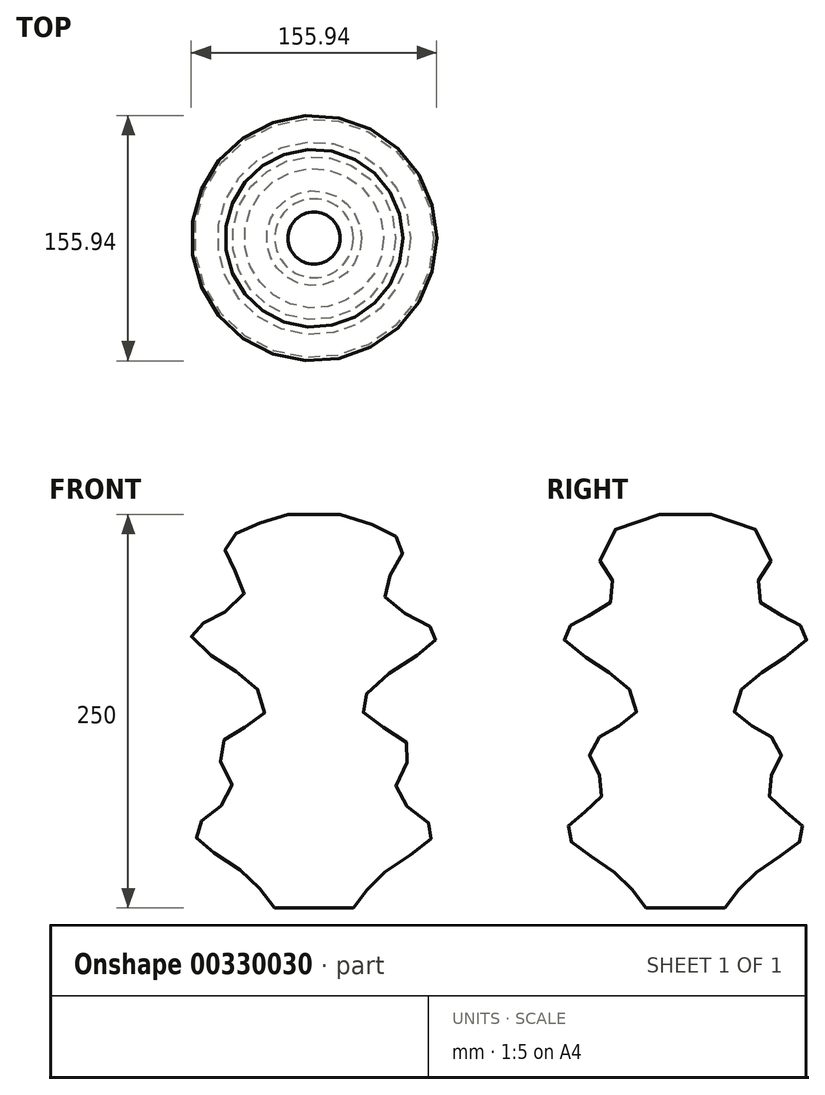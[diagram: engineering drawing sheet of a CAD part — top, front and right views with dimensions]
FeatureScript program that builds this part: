
annotation { "Feature Type Name" : "Feature", "Feature Type Description" : "" }
export const myFeature = defineFeature(function(context is Context, id is Id, definition is map)
    precondition{}
    {
        {
            var Q0;
            Q0=qCreatedBy(makeId("Top.planeOp"),FACE);
            cPlane(context, id + "F0", {"entities" : qUnion([Q0]), "cplaneType" : CPlaneType.OFFSET, "offset" : 25 * mm, "width" : 150 * mm, "height" : 150 * mm});
        }
        {
            var Q0;
            Q0=qCreatedBy(id+"F0.planeOp",FACE);
            cPlane(context, id + "F1", {"entities" : qUnion([Q0]), "cplaneType" : CPlaneType.OFFSET, "offset" : 25 * mm, "width" : 150 * mm, "height" : 150 * mm});
        }
        {
            var Q0;
            Q0=qCreatedBy(id+"F1.planeOp",FACE);
            cPlane(context, id + "F2", {"entities" : qUnion([Q0]), "cplaneType" : CPlaneType.OFFSET, "offset" : 25 * mm, "width" : 150 * mm, "height" : 150 * mm});
        }
        {
            var Q0;
            Q0=qCreatedBy(id+"F2.planeOp",FACE);
            cPlane(context, id + "F3", {"entities" : qUnion([Q0]), "cplaneType" : CPlaneType.OFFSET, "offset" : 25 * mm, "width" : 150 * mm, "height" : 150 * mm});
        }
        {
            var Q0;
            Q0=qCreatedBy(id+"F3.planeOp",FACE);
            cPlane(context, id + "F4", {"entities" : qUnion([Q0]), "cplaneType" : CPlaneType.OFFSET, "offset" : 25 * mm, "width" : 150 * mm, "height" : 150 * mm});
        }
        {
            var Q0;
            Q0=qCreatedBy(id+"F4.planeOp",FACE);
            cPlane(context, id + "F5", {"entities" : qUnion([Q0]), "cplaneType" : CPlaneType.OFFSET, "offset" : 25 * mm, "width" : 150 * mm, "height" : 150 * mm});
        }
        {
            var Q0;
            Q0=qCreatedBy(id+"F5.planeOp",FACE);
            cPlane(context, id + "F6", {"entities" : qUnion([Q0]), "cplaneType" : CPlaneType.OFFSET, "offset" : 25 * mm, "width" : 150 * mm, "height" : 150 * mm});
        }
        {
            var Q0;
            Q0=qCreatedBy(id+"F6.planeOp",FACE);
            cPlane(context, id + "F7", {"entities" : qUnion([Q0]), "cplaneType" : CPlaneType.OFFSET, "offset" : 25 * mm, "width" : 150 * mm, "height" : 150 * mm});
        }
        {
            var Q0;
            Q0=qCreatedBy(id+"F7.planeOp",FACE);
            cPlane(context, id + "F8", {"entities" : qUnion([Q0]), "cplaneType" : CPlaneType.OFFSET, "offset" : 25 * mm, "width" : 150 * mm, "height" : 150 * mm});
        }
        {
            var Q0;
            Q0=qCreatedBy(id+"F8.planeOp",FACE);
            cPlane(context, id + "F9", {"entities" : qUnion([Q0]), "cplaneType" : CPlaneType.OFFSET, "offset" : 25 * mm, "width" : 150 * mm, "height" : 150 * mm});
        }
        {
            var Q0;
            Q0=qCreatedBy(makeId("Top.planeOp"),FACE);
            var sketch = newSketch(context, id + "F10", { "sketchPlane" : qUnion([Q0])});
            skCircle(sketch, "E0", {"center": v(0, 0) * mm, "radius": 25 * mm});
            skSolve(sketch);
        }
        {
            var Q0;
            Q0=qCreatedBy(id+"F0.planeOp",FACE);
            var sketch = newSketch(context, id + "F11", { "sketchPlane" : qUnion([Q0])});
            skCircle(sketch, "E1", {"center": v(0, 0) * mm, "radius": 48 * mm});
            skSolve(sketch);
        }
        {
            var Q0;
            Q0=qCreatedBy(id+"F1.planeOp",FACE);
            var sketch = newSketch(context, id + "F12", { "sketchPlane" : qUnion([Q0])});
            skCircle(sketch, "E2", {"center": v(0, 0) * mm, "radius": 75.7 * mm});
            skSolve(sketch);
        }
        {
            var Q0;
            Q0=qCreatedBy(id+"F2.planeOp",FACE);
            var sketch = newSketch(context, id + "F13", { "sketchPlane" : qUnion([Q0])});
            skCircle(sketch, "E3", {"center": v(0, 0) * mm, "radius": 51.88 * mm});
            skSolve(sketch);
        }
        {
            var Q0;
            Q0=qCreatedBy(id+"F3.planeOp",FACE);
            var sketch = newSketch(context, id + "F14", { "sketchPlane" : qUnion([Q0])});
            skCircle(sketch, "E4", {"center": v(0, 0) * mm, "radius": 61.23 * mm});
            skSolve(sketch);
        }
        {
            var Q0;
            Q0=qCreatedBy(id+"F4.planeOp",FACE);
            var sketch = newSketch(context, id + "F15", { "sketchPlane" : qUnion([Q0])});
            skCircle(sketch, "E5", {"center": v(0, 0) * mm, "radius": 30.87 * mm});
            skSolve(sketch);
        }
        {
            var Q0;
            Q0=qCreatedBy(id+"F5.planeOp",FACE);
            var sketch = newSketch(context, id + "F16", { "sketchPlane" : qUnion([Q0])});
            skCircle(sketch, "E6", {"center": v(0, 0) * mm, "radius": 49.04 * mm});
            skSolve(sketch);
        }
        {
            var Q0;
            Q0=qCreatedBy(id+"F6.planeOp",FACE);
            var sketch = newSketch(context, id + "F17", { "sketchPlane" : qUnion([Q0])});
            skCircle(sketch, "E7", {"center": v(0, 0) * mm, "radius": 77.58 * mm});
            skSolve(sketch);
        }
        {
            var Q0;
            Q0=qCreatedBy(id+"F7.planeOp",FACE);
            var sketch = newSketch(context, id + "F18", { "sketchPlane" : qUnion([Q0])});
            skCircle(sketch, "E8", {"center": v(0, 0) * mm, "radius": 44.38 * mm});
            skSolve(sketch);
        }
        {
            var Q0;
            Q0=qCreatedBy(id+"F8.planeOp",FACE);
            var sketch = newSketch(context, id + "F19", { "sketchPlane" : qUnion([Q0])});
            skCircle(sketch, "E9", {"center": v(0, 0) * mm, "radius": 56.04 * mm});
            skSolve(sketch);
        }
        {
            var Q0;
            Q0=qCreatedBy(id+"F9.planeOp",FACE);
            var sketch = newSketch(context, id + "F20", { "sketchPlane" : qUnion([Q0])});
            skCircle(sketch, "E10", {"center": v(0, 0) * mm, "radius": 16.55 * mm});
            skSolve(sketch);
        }
        {
            var Q0;
            Q0=makeQuery(id+"F10.imprint","IMPRINT",FACE,{"disambiguationData":[TD([[makeQuery(id+"F10.imprint","IMPRINT",EDGE,{"derivedFrom":sQuery(id+"F10.wireOp",EDGE,"E0")}),1.0]])]});
            var Q1;
            Q1=makeQuery(id+"F11.imprint","IMPRINT",FACE,{"disambiguationData":[TD([[makeQuery(id+"F11.imprint","IMPRINT",EDGE,{"derivedFrom":sQuery(id+"F11.wireOp",EDGE,"E1")}),1.0]])]});
            var Q2;
            Q2=makeQuery(id+"F12.imprint","IMPRINT",FACE,{"disambiguationData":[TD([[makeQuery(id+"F12.imprint","IMPRINT",EDGE,{"derivedFrom":sQuery(id+"F12.wireOp",EDGE,"E2")}),1.0]])]});
            var Q3;
            Q3=makeQuery(id+"F13.imprint","IMPRINT",FACE,{"disambiguationData":[TD([[makeQuery(id+"F13.imprint","IMPRINT",EDGE,{"derivedFrom":sQuery(id+"F13.wireOp",EDGE,"E3")}),1.0]])]});
            var Q4;
            Q4=makeQuery(id+"F14.imprint","IMPRINT",FACE,{"disambiguationData":[TD([[makeQuery(id+"F14.imprint","IMPRINT",EDGE,{"derivedFrom":sQuery(id+"F14.wireOp",EDGE,"E4")}),1.0]])]});
            var Q5;
            Q5=makeQuery(id+"F15.imprint","IMPRINT",FACE,{"disambiguationData":[TD([[makeQuery(id+"F15.imprint","IMPRINT",EDGE,{"derivedFrom":sQuery(id+"F15.wireOp",EDGE,"E5")}),1.0]])]});
            var Q6;
            Q6=makeQuery(id+"F16.imprint","IMPRINT",FACE,{"disambiguationData":[TD([[makeQuery(id+"F16.imprint","IMPRINT",EDGE,{"derivedFrom":sQuery(id+"F16.wireOp",EDGE,"E6")}),1.0]])]});
            var Q7;
            Q7=makeQuery(id+"F17.imprint","IMPRINT",FACE,{"disambiguationData":[TD([[makeQuery(id+"F17.imprint","IMPRINT",EDGE,{"derivedFrom":sQuery(id+"F17.wireOp",EDGE,"E7")}),1.0]])]});
            var Q8;
            Q8=makeQuery(id+"F18.imprint","IMPRINT",FACE,{"disambiguationData":[TD([[makeQuery(id+"F18.imprint","IMPRINT",EDGE,{"derivedFrom":sQuery(id+"F18.wireOp",EDGE,"E8")}),1.0]])]});
            var Q9;
            Q9=makeQuery(id+"F19.imprint","IMPRINT",FACE,{"disambiguationData":[TD([[makeQuery(id+"F19.imprint","IMPRINT",EDGE,{"derivedFrom":sQuery(id+"F19.wireOp",EDGE,"E9")}),1.0]])]});
            var Q10;
            Q10=makeQuery(id+"F20.imprint","IMPRINT",FACE,{"disambiguationData":[TD([[makeQuery(id+"F20.imprint","IMPRINT",EDGE,{"derivedFrom":sQuery(id+"F20.wireOp",EDGE,"E10")}),1.0]])]});
            loft(context, id + "F21", {"sheetProfilesArray" : [{ "sheetProfileEntities" : qUnion([Q0]) }, { "sheetProfileEntities" : qUnion([Q1]) }, { "sheetProfileEntities" : qUnion([Q2]) }, { "sheetProfileEntities" : qUnion([Q3]) }, { "sheetProfileEntities" : qUnion([Q4]) }, { "sheetProfileEntities" : qUnion([Q5]) }, { "sheetProfileEntities" : qUnion([Q6]) }, { "sheetProfileEntities" : qUnion([Q7]) }, { "sheetProfileEntities" : qUnion([Q8]) }, { "sheetProfileEntities" : qUnion([Q9]) }, { "sheetProfileEntities" : qUnion([Q10]) }]});
        }
    });
